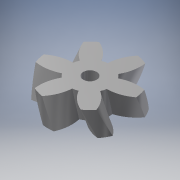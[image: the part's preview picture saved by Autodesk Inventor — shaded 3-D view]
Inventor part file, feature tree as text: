
AUTODESK INVENTOR PART (.ipt)
format: ipt  version: 2017 SP1 (Build 210196100, 196)  size: 559,104 bytes
history: native  units: mm (DEFAULTED — no unit token found)
features: sketch x4, plane x3, other x3, extrude x2
ambient origin geometry x8: Origin, YZ Plane, XZ Plane, XY Plane, X Axis, Y Axis, Z Axis, Center Point
bodies: Solid1 (feature_tree)
feature tree (12):
  extrude  "Extrusion1"  Depth=10.0mm TaperAngle=0.0deg
  plane  "Work Plane2"
  plane  "Work Plane8"
  plane  "Work Plane9"
  other  "Engrenage cylindrique"
  sketch  "Esquisse 3D1"
  extrude  "Extrusion2"  Depth=10.0mm TaperAngle=0.0deg
  sketch  "Sketch1"  dims[d0=34.188431mm d1=10.0mm d2=0.0mm]
  sketch  "Sketch2"  dims[d3=26.24881mm d4=10.0mm d5=0.0mm d16=26.24881mm d17=0.0mm d34=30.0deg d39=0.0mm d41=0.0mm d43=26.24881mm d46=26.24881mm d47=0.0mm d48=0.0mm d49=5.5mm d50=20.0mm d51=0.0mm]
  other  "Srf1"
  sketch  "Esquisse3"
  other  "Diamètre primitif"
